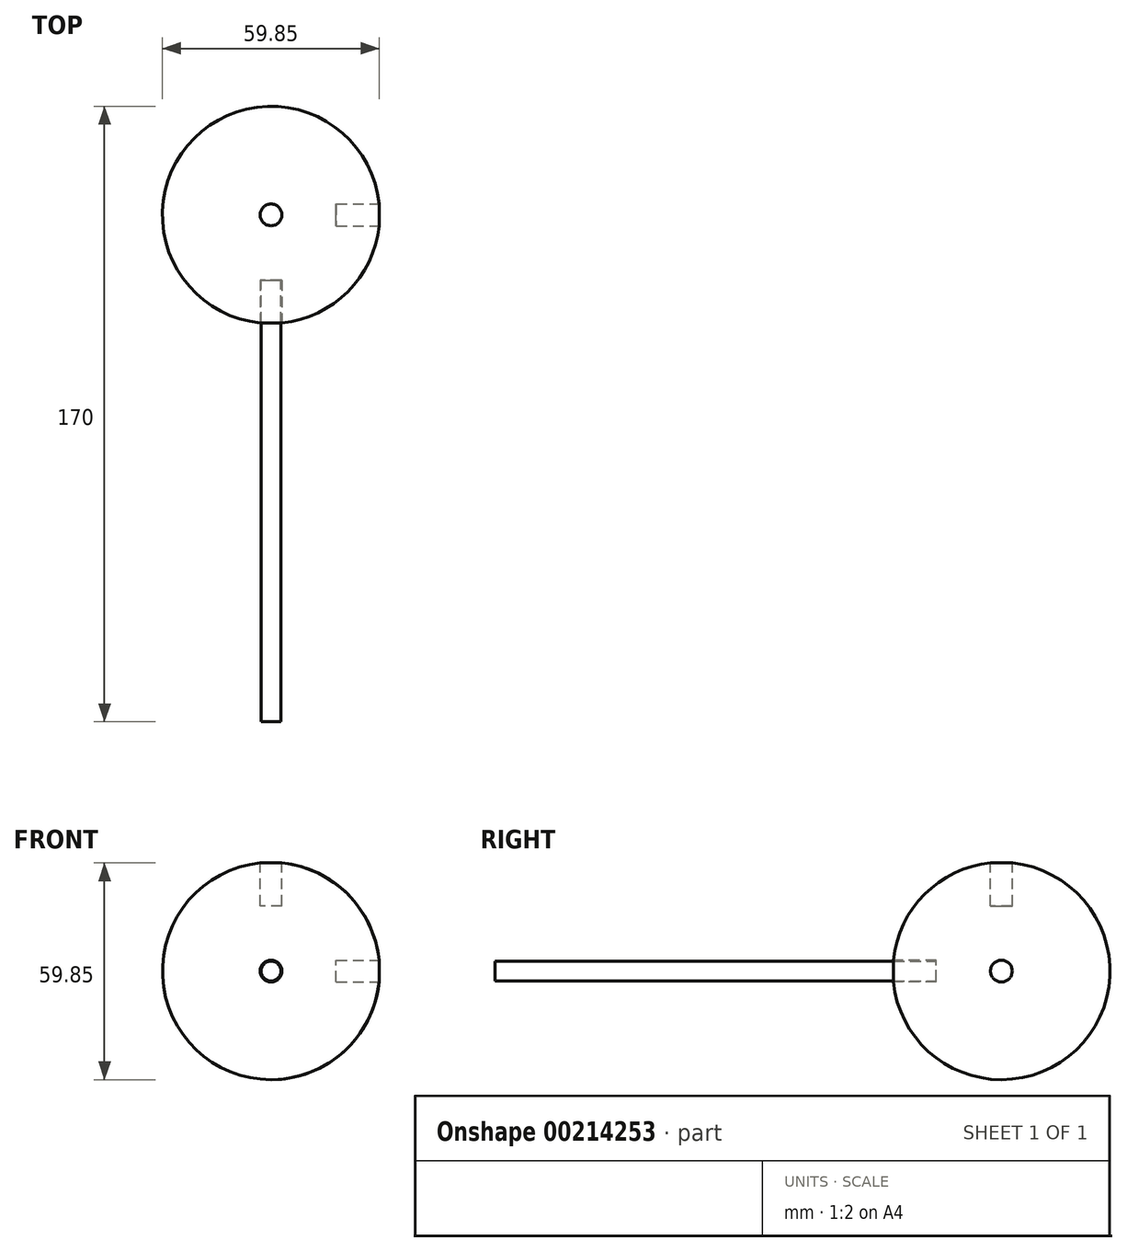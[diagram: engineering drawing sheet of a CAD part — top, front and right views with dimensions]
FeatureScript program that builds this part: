
annotation { "Feature Type Name" : "Feature", "Feature Type Description" : "" }
export const myFeature = defineFeature(function(context is Context, id is Id, definition is map)
    precondition{}
    {
        {
            assignVariable(context, id + "F0", {"name" : "D", "anyValue" : 60});
        }
        {
            assignVariable(context, id + "F1", {"name" : "d", "anyValue" : 6});
        }
        {
            assignVariable(context, id + "F2", {"name" : "L", "anyValue" : 122});
        }
        {
            var Q0;
            Q0=qCreatedBy(makeId("Front.planeOp"),FACE);
            var sketch = newSketch(context, id + "F3", { "sketchPlane" : qUnion([Q0])});
            skArc(sketch, "E0", {"start": v(0, -30) * mm, "mid": v(-30, 0) * mm, "end": v(0, 30) * mm});
            skLineSegment(sketch, "E1", {"start": v(0, 30) * mm, "end": v(0, -30) * mm});
            skSolve(sketch);
        }
        {
            var Q0;
            Q0 = qSketchRegion(id + "F3", true);
            var Q1;
            Q1=sQuery(id+"F3.wireOp",EDGE,"E1");
            revolve(context, id + "F4", {"entities" : qUnion([Q0]), "axis" : qUnion([Q1]), "revolveType" : RevolveType.FULL});
        }
        {
            var Q0;
            Q0=qCreatedBy(makeId("Front.planeOp"),FACE);
            cPlane(context, id + "F5", {"entities" : qUnion([Q0]), "cplaneType" : CPlaneType.OFFSET, "offset" : (getVariable(context, 'D') / 2) * mm, "width" : 150 * mm, "height" : 150 * mm});
        }
        {
            var Q0;
            Q0=qCreatedBy(id+"F5.planeOp",FACE);
            var sketch = newSketch(context, id + "F6", { "sketchPlane" : qUnion([Q0])});
            skCircle(sketch, "E2", {"center": v(0, 0) * mm, "radius": 3 * mm});
            skSolve(sketch);
        }
        {
            var Q0;
            Q0 = qSketchRegion(id + "F6", true);
            extrude(context, id + "F7", {"entities" : qUnion([Q0]), "operationType" : NewBodyOperationType.REMOVE, "oppositeDirection" : true, "depth" : (getVariable(context, 'd') * 2) * mm});
        }
        {
            var Q0;
            Q0=qCreatedBy(makeId("Right.planeOp"),FACE);
            cPlane(context, id + "F8", {"entities" : qUnion([Q0]), "cplaneType" : CPlaneType.OFFSET, "offset" : (getVariable(context, 'D') / 2) * mm, "width" : 150 * mm, "height" : 150 * mm});
        }
        {
            var Q0;
            Q0=qCreatedBy(id+"F8.planeOp",FACE);
            var sketch = newSketch(context, id + "F9", { "sketchPlane" : qUnion([Q0])});
            skCircle(sketch, "E3", {"center": v(0, 0) * mm, "radius": 3 * mm});
            skSolve(sketch);
        }
        {
            var Q0;
            Q0 = qSketchRegion(id + "F9", true);
            extrude(context, id + "F10", {"entities" : qUnion([Q0]), "operationType" : NewBodyOperationType.REMOVE, "oppositeDirection" : true, "depth" : (getVariable(context, 'd') * 2) * mm});
        }
        {
            var Q0;
            Q0=qCreatedBy(makeId("Top.planeOp"),FACE);
            cPlane(context, id + "F11", {"entities" : qUnion([Q0]), "cplaneType" : CPlaneType.OFFSET, "offset" : (getVariable(context, 'D') / 2) * mm, "width" : 150 * mm, "height" : 150 * mm});
        }
        {
            var Q0;
            Q0=qCreatedBy(id+"F11.planeOp",FACE);
            var sketch = newSketch(context, id + "F12", { "sketchPlane" : qUnion([Q0])});
            skCircle(sketch, "E4", {"center": v(0, 0) * mm, "radius": 3 * mm});
            skSolve(sketch);
        }
        {
            var Q0;
            Q0 = qSketchRegion(id + "F12", true);
            extrude(context, id + "F13", {"entities" : qUnion([Q0]), "operationType" : NewBodyOperationType.REMOVE, "oppositeDirection" : true, "depth" : (getVariable(context, 'd') * 2) * mm});
        }
        {
            var Q0;
            Q0=makeQuery(id+"F7.boolean.opBoolean","COPY",FACE,{"derivedFrom":makeQuery(id+"F7.opExtrude","CAP_FACE",FACE,{"disambiguationData":[OSD([sQuery(id+"F6.wireOp",EDGE,"E2")])],"isStart":false})});
            var sketch = newSketch(context, id + "F14", { "sketchPlane" : qUnion([Q0])});
            skCircle(sketch, "E5", {"center": v(0, 0) * mm, "radius": 2.75 * mm});
            skSolve(sketch);
        }
        {
            var Q0;
            Q0 = qSketchRegion(id + "F14", true);
            extrude(context, id + "F15", {"entities" : qUnion([Q0]), "depth" : (getVariable(context, 'L')) * mm});
        }
    });
